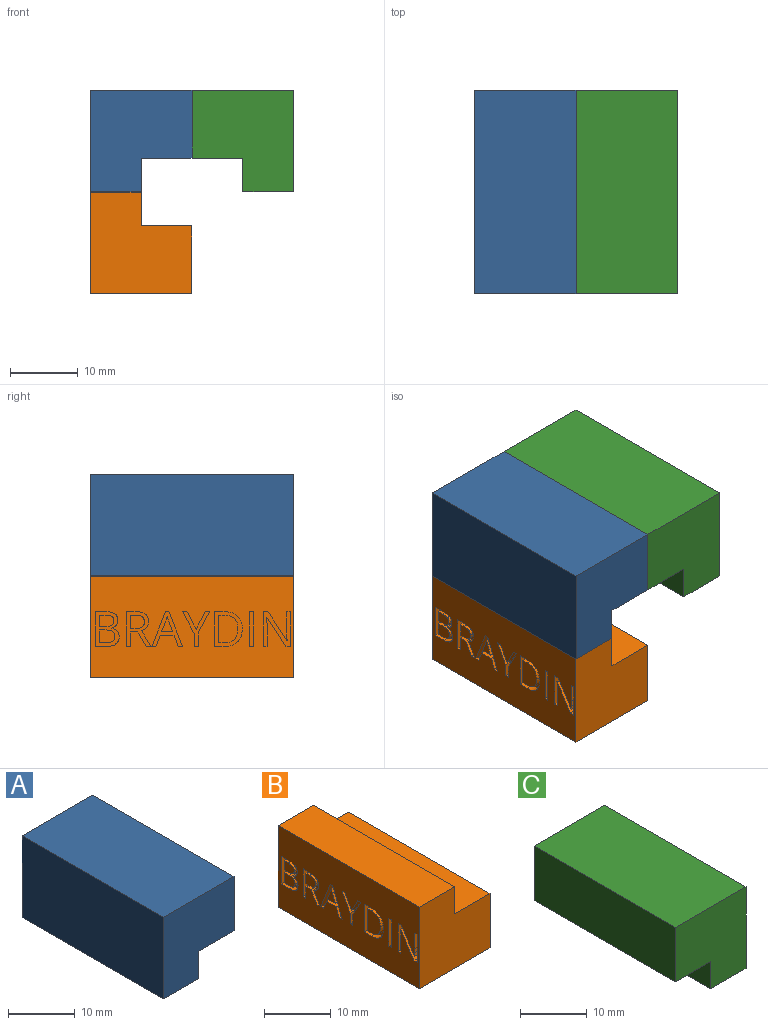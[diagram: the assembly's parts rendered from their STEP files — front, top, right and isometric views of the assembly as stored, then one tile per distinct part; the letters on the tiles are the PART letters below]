
ASSEMBLY  parts=3 mates=1
PART A: 8 faces, bbox 15x30x15 mm
  f0: plane 30x15mm, normal (0,0,1), area 450mm2, adj f1,f2,f3,f6
  f1: plane 30x15mm, normal (-1,0,0), area 450mm2, adj f0,f2,f3,f5
  f2: plane 15x15mm, normal (0,-1,0), area 187.5mm2, adj f0,f1,f4,f5,f6,f7
  f3: plane 15x15mm, normal (0,1,0), area 187.5mm2, adj f0,f1,f4,f5,f6,f7
  f4: plane 30x5mm, normal (1,0,0), area 150mm2, adj f2,f3,f5,f7
  f5: plane 30x7.5mm, normal (0,0,-1), area 225mm2, adj f1,f2,f3,f4
  f6: plane 30x10mm, normal (1,0,0), area 300mm2, adj f0,f2,f3,f7
  f7: plane 30x7.5mm, normal (0,0,-1), area 225mm2, adj f2,f3,f4,f6
PART B: 118 faces, bbox 15x30x15 mm
  f0: plane 30x15mm, normal (-1,0,0), area 378.6mm2, adj f1,f3,f4,f7,f8,f9,f10,f11
  f1: plane 15x15mm, normal (0,-1,0), area 187.5mm2, adj f0,f2,f4,f5,f6,f7
  f2: plane 30x5mm, normal (1,0,0), area 150mm2, adj f1,f3,f6,f7
  f3: plane 15x15mm, normal (0,1,0), area 187.5mm2, adj f0,f2,f4,f5,f6,f7
  f4: plane 30x15mm, normal (0,0,-1), area 450mm2, adj f0,f1,f3,f5
  f5: plane 30x10mm, normal (1,0,0), area 300mm2, adj f1,f3,f4,f6
  f6: plane 30x7.5mm, normal (0,0,1), area 225mm2, adj f1,f2,f3,f5
  f7: plane 30x7.5mm, normal (0,0,1), area 225mm2, adj f0,f1,f2,f3
  f8: plane 2.56x1.36mm, normal (0,-0.88,-0.47), area 2.9mm2, adj f0,f9,f16,f17
  f9: plane 2.56x1.35mm, normal (0,0.88,-0.47), area 2.9mm2, adj f0,f8,f10,f17
  f10: plane 1x0.65mm, normal (0,0,-1), area 0.7mm2, adj f0,f9,f11,f17
  f11: plane 3.16x1.7mm, normal (0,-0.88,0.47), area 3.6mm2, adj f0,f10,f12,f17
  f12: plane 1.96x1mm, normal (0,-1,0), area 2mm2, adj f0,f11,f13,f17
  f13: plane 1x0.6mm, normal (0,0,1), area 0.6mm2, adj f0,f12,f14,f17
  f14: plane 1.98x1mm, normal (0,1,0), area 2mm2, adj f0,f13,f15,f17
  f15: plane 3.13x1.71mm, normal (0,0.88,0.48), area 3.6mm2, adj f0,f14,f16,f17
  f16: plane 1x0.64mm, normal (0,0,-1), area 0.6mm2, adj f0,f8,f15,f17
  f17: plane 5.11x4.01mm, normal (-1,0,0), area 5mm2, adj f8,f9,f10,f11,f12,f13,f14,f15
  f18: plane 1.91x1mm, normal (0,1,0), area 1.9mm2, adj f19,f42,f43,f114
  f19: plane 1.02x1mm, normal (0,0,1), area 1mm2, adj f18,f20,f43,f114
  f20: extruded ~1x0.97mm, area 1mm2, adj f19,f21,f43,f114
  f21: extruded ~1x0.7mm, area 0.8mm2, adj f20,f22,f43,f114
  f22: extruded ~1x0.75mm, area 0.8mm2, adj f21,f23,f43,f114
  f23: extruded ~1x0.93mm, area 1mm2, adj f22,f42,f43,f114
  f24: plane 1x0.98mm, normal (0,0,-1), area 1mm2, adj f25,f40,f43,f44
  f25: plane 1.67x1mm, normal (0,1,0), area 1.7mm2, adj f24,f26,f43,f44
  f26: plane 1x0.88mm, normal (0,0,1), area 0.9mm2, adj f25,f27,f43,f44
  f27: extruded ~1x0.98mm, area 1mm2, adj f26,f28,f43,f44
  f28: extruded ~1x0.62mm, area 0.7mm2, adj f27,f29,f43,f44
  f29: extruded ~1x0.67mm, area 0.8mm2, adj f28,f40,f43,f44
  f30: plane 1.45x1mm, normal (0,0,-1), area 1.4mm2, adj f0,f31,f41,f43
  f31: plane 5.11x1mm, normal (0,-1,0), area 5.1mm2, adj f0,f30,f32,f43
  f32: plane 1.78x1mm, normal (0,0,1), area 1.8mm2, adj f0,f31,f33,f43
  f33: extruded ~1.3x1mm, area 1.4mm2, adj f0,f32,f34,f43
  f34: extruded ~1.07x1mm, area 1.2mm2, adj f0,f33,f35,f43
  f35: extruded ~1.22x1.17mm, area 1.9mm2, adj f0,f34,f36,f43
  f36: plane 1x0.03mm, normal (0,1,0), area 0mm2, adj f0,f35,f37,f43
  f37: extruded ~1x0.74mm, area 0.9mm2, adj f0,f36,f38,f43
  f38: extruded ~1x0.75mm, area 0.8mm2, adj f0,f37,f39,f43
  f39: extruded ~1x0.96mm, area 1.1mm2, adj f0,f38,f41,f43
  f40: extruded ~1x0.91mm, area 0.9mm2, adj f24,f29,f43,f44
  f41: extruded ~1.47x1mm, area 1.5mm2, adj f0,f30,f39,f43
  f42: plane 1.07x1mm, normal (0,0,-1), area 1.1mm2, adj f18,f23,f43,f114
  f43: plane 5.11x3.54mm, normal (-1,0,0), area 8.9mm2, adj f18,f19,f20,f21,f22,f23,f24,f25
  f44: plane 2.16x1.67mm, normal (-1,0,0), area 3.3mm2, adj f24,f25,f26,f27,f28,f29,f40
  f45: extruded ~1.51x1mm, area 1.6mm2, adj f46,f58,f59,f115
  f46: extruded ~1.55x1mm, area 1.7mm2, adj f45,f47,f59,f115
  f47: extruded ~1.6x1mm, area 1.7mm2, adj f46,f48,f59,f115
  f48: plane 1x0.72mm, normal (0,0,-1), area 0.7mm2, adj f47,f49,f59,f115
  f49: plane 4.09x1mm, normal (0,1,0), area 4.1mm2, adj f48,f50,f59,f115
  f50: plane 1x0.86mm, normal (0,0,1), area 0.9mm2, adj f49,f58,f59,f115
  f51: extruded ~1.94x1mm, area 2.1mm2, adj f0,f52,f57,f59
  f52: extruded ~1.85x1mm, area 2mm2, adj f0,f51,f53,f59
  f53: extruded ~1.85x1mm, area 2mm2, adj f0,f52,f54,f59
  f54: plane 1.57x1mm, normal (0,0,-1), area 1.6mm2, adj f0,f53,f55,f59
  f55: plane 5.11x1mm, normal (0,-1,0), area 5.1mm2, adj f0,f54,f56,f59
  f56: plane 1.42x1mm, normal (0,0,1), area 1.4mm2, adj f0,f55,f57,f59
  f57: extruded ~1.98x1mm, area 2.1mm2, adj f0,f51,f56,f59
  f58: extruded ~1.49x1mm, area 1.6mm2, adj f45,f50,f59,f115
  f59: plane 5.11x4.08mm, normal (-1,0,0), area 8.3mm2, adj f45,f46,f47,f48,f49,f50,f51,f52
  f60: plane 1.59x1mm, normal (0,-0.94,0.35), area 1.7mm2, adj f61,f72,f73,f116
  f61: plane 1.65x1mm, normal (0,0,-1), area 1.7mm2, adj f60,f62,f73,f116
  f62: plane 1.59x1mm, normal (0,0.94,0.35), area 1.7mm2, adj f61,f63,f73,f116
  f63: extruded ~1x0.74mm, area 0.8mm2, adj f62,f72,f73,f116
  f64: plane 1.63x1mm, normal (0,-0.93,0.36), area 1.7mm2, adj f0,f65,f71,f73
  f65: plane 1x0.62mm, normal (0,0,1), area 0.6mm2, adj f0,f64,f66,f73
  f66: plane 5.14x2.01mm, normal (0,0.93,-0.36), area 5.5mm2, adj f0,f65,f67,f73
  f67: plane 1x0.5mm, normal (0,0,-1), area 0.5mm2, adj f0,f66,f68,f73
  f68: plane 5.14x2.02mm, normal (0,-0.93,-0.37), area 5.5mm2, adj f0,f67,f69,f73
  f69: plane 1x0.6mm, normal (0,0,1), area 0.6mm2, adj f0,f68,f70,f73
  f70: plane 1.63x1mm, normal (0,0.93,0.36), area 1.7mm2, adj f0,f69,f71,f73
  f71: plane 2.05x1mm, normal (0,0,1), area 2mm2, adj f0,f64,f70,f73
  f72: extruded ~1x0.74mm, area 0.8mm2, adj f60,f63,f73,f116
  f73: plane 5.14x4.53mm, normal (-1,0,0), area 6.7mm2, adj f60,f61,f62,f63,f64,f65,f66,f67
  f74: plane 1x0.82mm, normal (0,0,-1), area 0.8mm2, adj f75,f91,f92,f117
  f75: plane 1.96x1mm, normal (0,1,0), area 2mm2, adj f74,f76,f92,f117
  f76: plane 1x0.77mm, normal (0,0,1), area 0.8mm2, adj f75,f77,f92,f117
  f77: extruded ~1x0.96mm, area 1mm2, adj f76,f78,f92,f117
  f78: extruded ~1x0.73mm, area 0.8mm2, adj f77,f79,f92,f117
  f79: extruded ~1x0.75mm, area 0.8mm2, adj f78,f91,f92,f117
  f80: plane 2.13x1mm, normal (0,1,0), area 2.1mm2, adj f0,f81,f90,f92
  f81: plane 1.07x1mm, normal (0,0,1), area 1.1mm2, adj f0,f80,f82,f92
  f82: plane 2.13x1.24mm, normal (0,-0.86,0.5), area 2.5mm2, adj f0,f81,f83,f92
  f83: plane 1x0.7mm, normal (0,0,1), area 0.7mm2, adj f0,f82,f84,f92
  f84: plane 2.3x1.39mm, normal (0,0.86,-0.52), area 2.7mm2, adj f0,f83,f85,f92
  f85: extruded ~1.37x1.03mm, area 1.8mm2, adj f0,f84,f86,f92
  f86: extruded ~1.08x1mm, area 1.2mm2, adj f0,f85,f87,f92
  f87: extruded ~1.39x1mm, area 1.5mm2, adj f0,f86,f88,f92
  f88: plane 1.4x1mm, normal (0,0,-1), area 1.4mm2, adj f0,f87,f89,f92
  f89: plane 5.11x1mm, normal (0,-1,0), area 5.1mm2, adj f0,f88,f90,f92
  f90: plane 1x0.59mm, normal (0,0,1), area 0.6mm2, adj f0,f80,f89,f92
  f91: extruded ~1x0.92mm, area 1mm2, adj f74,f79,f92,f117
  f92: plane 5.11x3.6mm, normal (-1,0,0), area 7.8mm2, adj f74,f75,f76,f77,f78,f79,f80,f81
  f93: plane 1x0.68mm, normal (0,0,1), area 0.7mm2, adj f0,f94,f107,f108
  f94: plane 5.11x1mm, normal (0,1,0), area 5.1mm2, adj f0,f93,f95,f108
  f95: plane 1x0.56mm, normal (0,0,-1), area 0.6mm2, adj f0,f94,f96,f108
  f96: plane 2.94x1mm, normal (0,-1,0), area 2.9mm2, adj f0,f95,f97,f108
  f97: extruded ~1x0.73mm, area 0.7mm2, adj f0,f96,f98,f108
  f98: extruded ~1x0.61mm, area 0.6mm2, adj f0,f97,f99,f108
  f99: plane 1x0.03mm, normal (0,0,-1), area 0mm2, adj f0,f98,f100,f108
  f100: plane 4.28x2.79mm, normal (0,0.84,-0.55), area 5.1mm2, adj f0,f99,f101,f108
  f101: plane 1x0.67mm, normal (0,0,-1), area 0.7mm2, adj f0,f100,f102,f108
  f102: plane 5.11x1mm, normal (0,-1,0), area 5.1mm2, adj f0,f101,f103,f108
  f103: plane 1x0.55mm, normal (0,0,1), area 0.5mm2, adj f0,f102,f104,f108
  f104: plane 2.91x1mm, normal (0,1,0), area 2.9mm2, adj f0,f103,f105,f108
  f105: extruded ~1.38x1mm, area 1.4mm2, adj f0,f104,f106,f108
  f106: plane 1x0.03mm, normal (0,0,1), area 0mm2, adj f0,f105,f107,f108
  f107: plane 4.29x2.8mm, normal (0,-0.84,0.55), area 5.1mm2, adj f0,f93,f106,f108
  f108: plane 5.11x4mm, normal (-1,0,0), area 8.6mm2, adj f93,f94,f95,f96,f97,f98,f99,f100
  f109: plane 5.11x1mm, normal (0,-1,0), area 5.1mm2, adj f0,f110,f112,f113
  f110: plane 1x0.59mm, normal (0,0,1), area 0.6mm2, adj f0,f109,f111,f113
  f111: plane 5.11x1mm, normal (0,1,0), area 5.1mm2, adj f0,f110,f112,f113
  f112: plane 1x0.59mm, normal (0,0,-1), area 0.6mm2, adj f0,f109,f111,f113
  f113: plane 5.11x0.59mm, normal (-1,0,0), area 3mm2, adj f109,f110,f111,f112
  f114: plane 2.31x1.91mm, normal (-1,0,0), area 4mm2, adj f18,f19,f20,f21,f22,f23,f42
  f115: plane 4.09x2.86mm, normal (-1,0,0), area 10.3mm2, adj f45,f46,f47,f48,f49,f50,f58
  f116: plane 2.32x1.65mm, normal (-1,0,0), area 1.8mm2, adj f60,f61,f62,f63,f72
  f117: plane 2.03x1.96mm, normal (-1,0,0), area 3.6mm2, adj f74,f75,f76,f77,f78,f79,f91
PART C: 8 faces, bbox 15x30x15 mm
  f0: plane 30x15mm, normal (0,0,1), area 450mm2, adj f1,f2,f3,f5
  f1: plane 15x15mm, normal (0,-1,0), area 187.5mm2, adj f0,f3,f4,f5,f6,f7
  f2: plane 15x15mm, normal (0,1,0), area 187.5mm2, adj f0,f3,f4,f5,f6,f7
  f3: plane 30x15mm, normal (1,0,0), area 450mm2, adj f0,f1,f2,f4
  f4: plane 30x7.5mm, normal (0,0,-1), area 225mm2, adj f1,f2,f3,f6
  f5: plane 30x10mm, normal (-1,0,0), area 300mm2, adj f0,f1,f2,f7
  f6: plane 30x5mm, normal (-1,0,0), area 150mm2, adj f1,f2,f4,f7
  f7: plane 30x7.5mm, normal (0,0,-1), area 225mm2, adj f1,f2,f5,f6
PLACE A at identity
PLACE B t=(10.37,0,-7.03)mm
PLACE C at identity
MATE parallel B.f7 <-> A.f5  axis (0,0,1) through (-45.93,-15,25.5)mm
